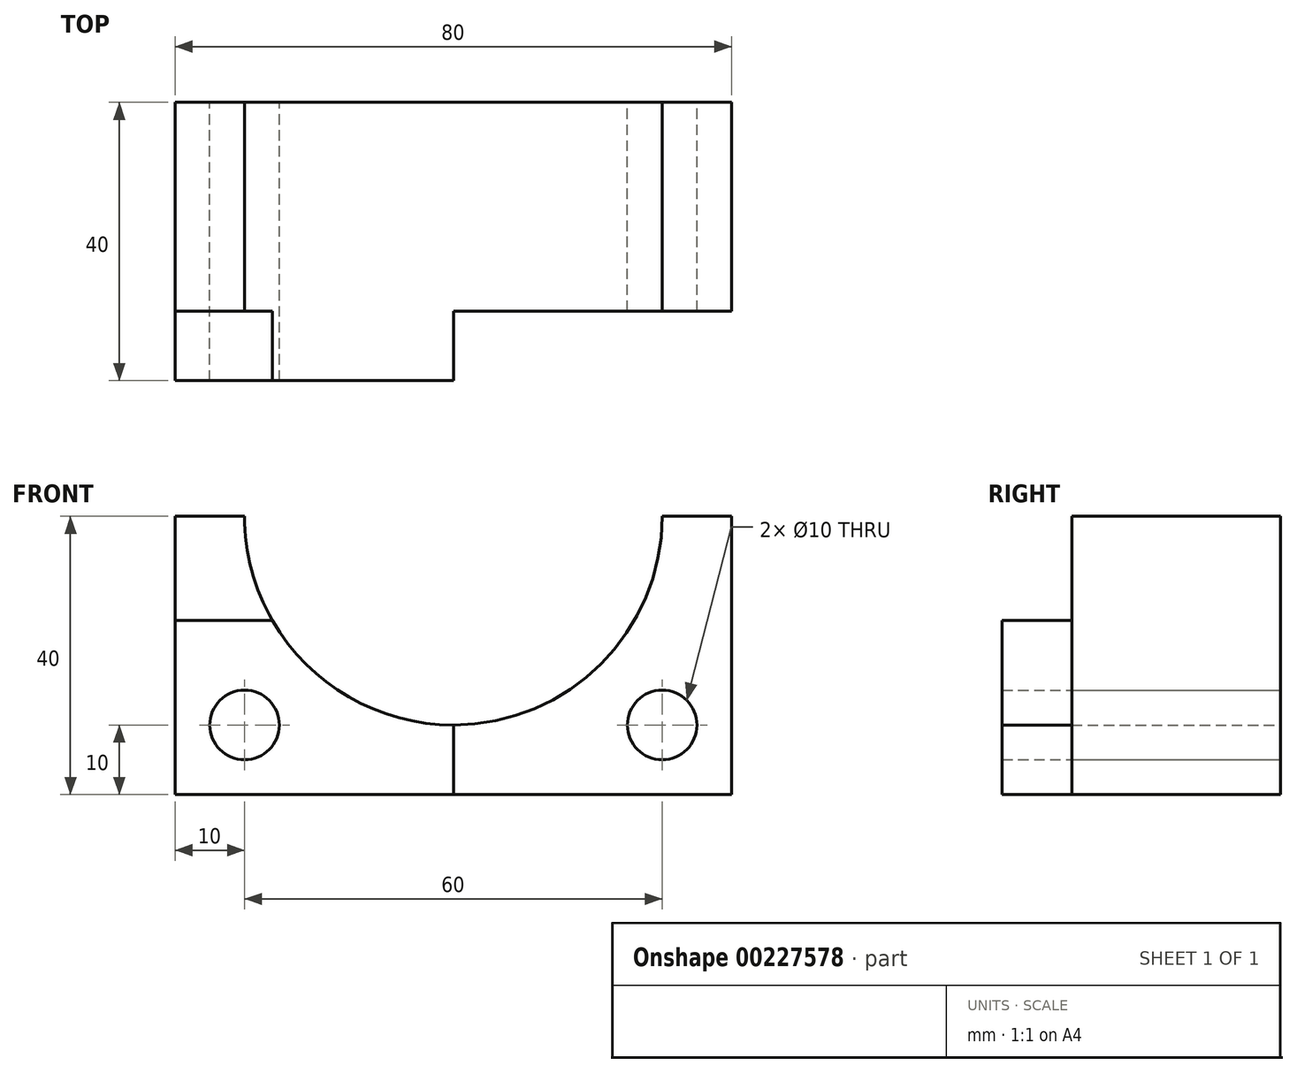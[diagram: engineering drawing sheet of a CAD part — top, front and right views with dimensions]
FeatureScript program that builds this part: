
annotation { "Feature Type Name" : "Feature", "Feature Type Description" : "" }
export const myFeature = defineFeature(function(context is Context, id is Id, definition is map)
    precondition{}
    {
        {
            var Q0;
            Q0=qCreatedBy(makeId("Front.planeOp"),FACE);
            var sketch = newSketch(context, id + "F0", { "sketchPlane" : qUnion([Q0])});
            skLineSegment(sketch, "E0.bottom", {"start": v(-80, 40) * mm, "end": v(-70, 40) * mm});
            skLineSegment(sketch, "E0.top", {"start": v(-80, 0) * mm, "end": v(0, 0) * mm});
            skLineSegment(sketch, "E0.left", {"start": v(-80, 40) * mm, "end": v(-80, 0) * mm});
            skLineSegment(sketch, "E0.right", {"start": v(0, 40) * mm, "end": v(0, 0) * mm});
            skArc(sketch, "E1", {"start": v(-70, 40) * mm, "mid": v(-40, 10) * mm, "end": v(-10, 40) * mm});
            skCircle(sketch, "E2", {"center": v(-70, 10) * mm, "radius": 5 * mm});
            skCircle(sketch, "E3", {"center": v(-10, 10) * mm, "radius": 5 * mm});
            skLineSegment(sketch, "E4", {"start": v(-80, 25) * mm, "end": v(-65.98, 25) * mm});
            skLineSegment(sketch, "E5.trimOffspring", {"start": v(-10, 40) * mm, "end": v(0, 40) * mm});
            skLineSegment(sketch, "E6", {"start": v(-40, 10) * mm, "end": v(-40, 0) * mm});
            skSolve(sketch);
        }
        {
            var Q0;
            Q0=makeQuery(id+"F0.imprint","IMPRINT",FACE,{"disambiguationData":[TD([[makeQuery(id+"F0.imprint","IMPRINT",EDGE,{"derivedFrom":sQuery(id+"F0.wireOp",EDGE,"E2")}),-1.0]])]});
            extrude(context, id + "F1", {"entities" : qUnion([Q0]), "depth" : 40 * mm});
        }
        {
            var Q0;
            {var subQ3=sQuery(id+"F0.wireOp",EDGE,"E0.right");Q0=makeQuery(id+"F0.imprint","IMPRINT",FACE,{"disambiguationData":[TD([[makeQuery(id+"F0.imprint","IMPRINT",EDGE,{"derivedFrom":subQ3}),-1.0]])]});}
            var Q1;
            {var subQ0=sQuery(id+"F0.wireOp",EDGE,"E0.bottom");Q1=makeQuery(id+"F0.imprint","IMPRINT",FACE,{"disambiguationData":[TD([[makeQuery(id+"F0.imprint","IMPRINT",EDGE,{"derivedFrom":subQ0}),-1.0]])]});}
            extrude(context, id + "F2", {"entities" : qUnion([Q0, Q1]), "operationType" : NewBodyOperationType.ADD, "depth" : 30 * mm});
        }
    });
